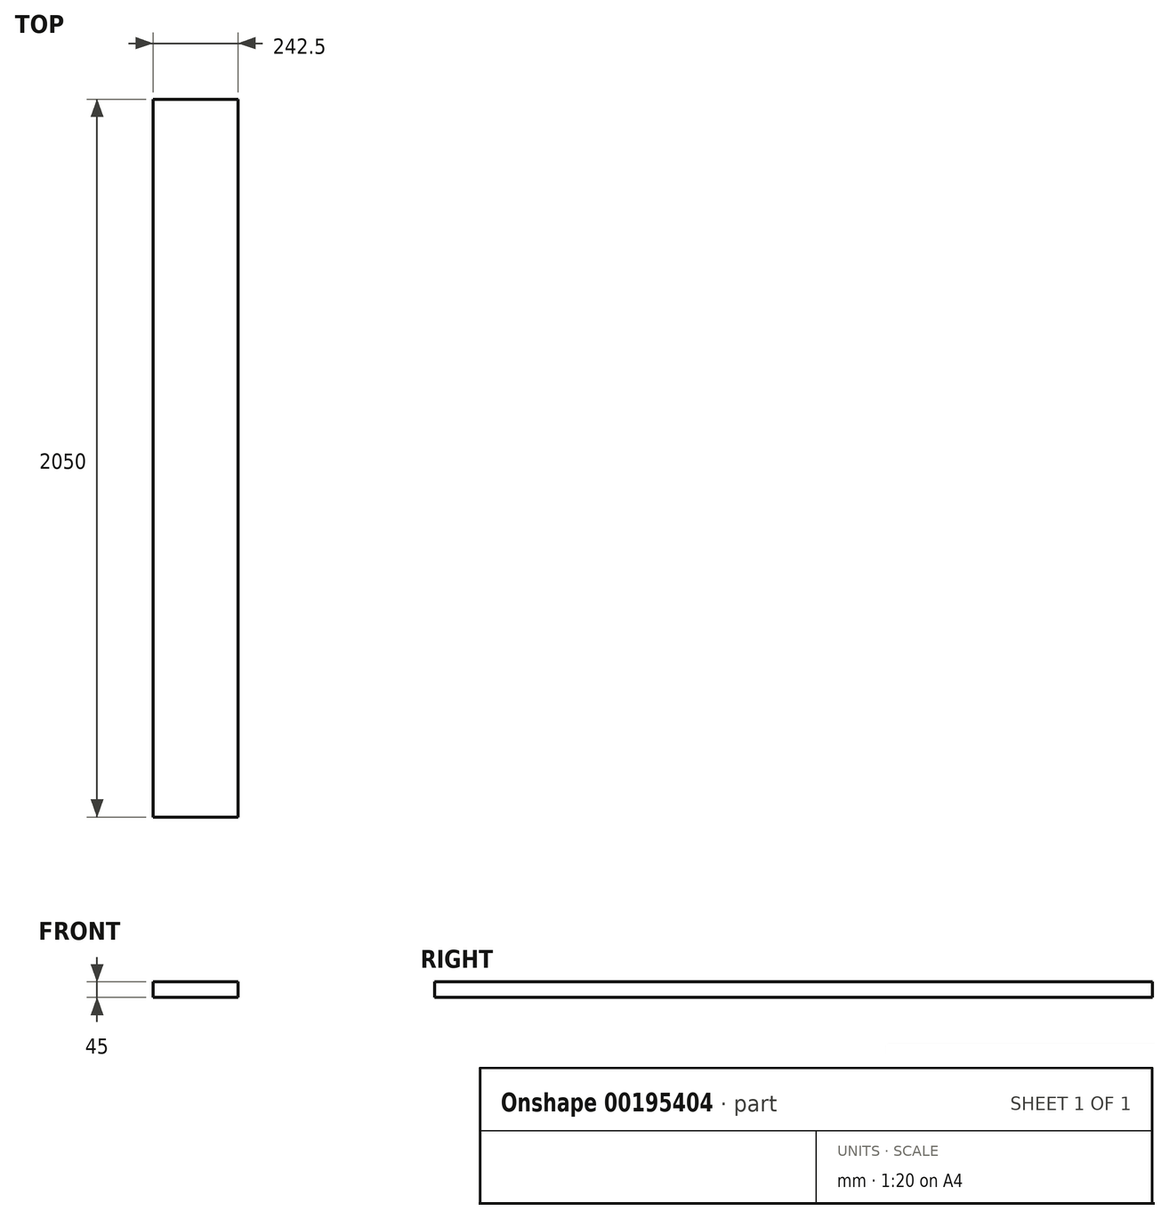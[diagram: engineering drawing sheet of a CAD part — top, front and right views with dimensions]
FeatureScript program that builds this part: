
annotation { "Feature Type Name" : "Feature", "Feature Type Description" : "" }
export const myFeature = defineFeature(function(context is Context, id is Id, definition is map)
    precondition{}
    {
        {
            var Q0;
            Q0=qCreatedBy(makeId("Top.planeOp"),FACE);
            var sketch = newSketch(context, id + "F0", { "sketchPlane" : qUnion([Q0])});
            skLineSegment(sketch, "E0.bottom", {"start": v(-121.25, 1025) * mm, "end": v(121.25, 1025) * mm});
            skLineSegment(sketch, "E0.top", {"start": v(-121.25, -1025) * mm, "end": v(121.25, -1025) * mm});
            skLineSegment(sketch, "E0.left", {"start": v(-121.25, 1025) * mm, "end": v(-121.25, -1025) * mm});
            skLineSegment(sketch, "E0.right", {"start": v(121.25, 1025) * mm, "end": v(121.25, -1025) * mm});
            skPoint(sketch, "E0.middle", {"position": v(0, 0) * mm});
            skSolve(sketch);
        }
        {
            var Q0;
            Q0 = qSketchRegion(id + "F0", true);
            extrude(context, id + "F1", {"entities" : qUnion([Q0]), "depth" : 45 * mm});
        }
    });
